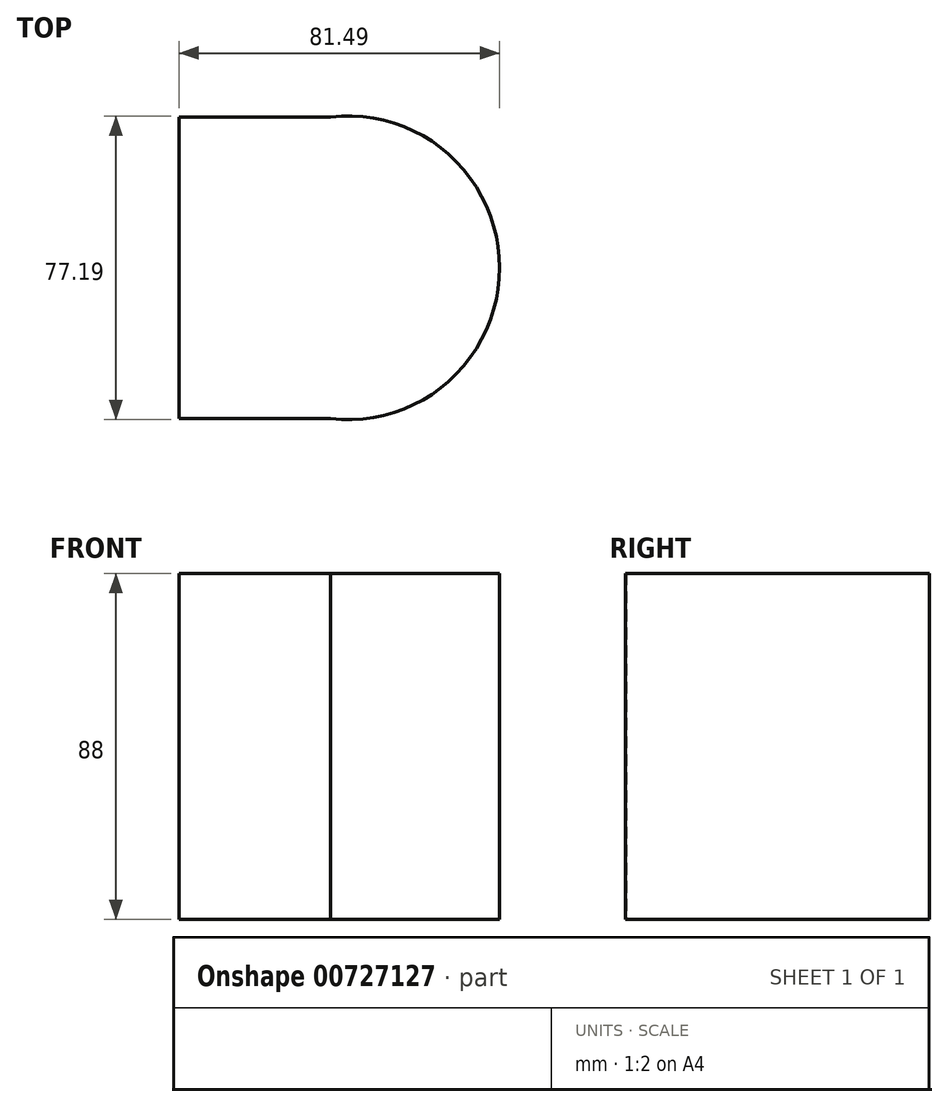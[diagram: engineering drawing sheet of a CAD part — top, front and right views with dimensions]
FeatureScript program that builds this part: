
annotation { "Feature Type Name" : "Feature", "Feature Type Description" : "" }
export const myFeature = defineFeature(function(context is Context, id is Id, definition is map)
    precondition{}
    {
        {
            var Q0;
            Q0=qCreatedBy(makeId("Top.planeOp"),FACE);
            var sketch = newSketch(context, id + "F0", { "sketchPlane" : qUnion([Q0])});
            skLineSegment(sketch, "E0.bottom", {"start": v(0, 0) * mm, "end": v(42.9, 0) * mm});
            skLineSegment(sketch, "E0.top", {"start": v(0, 76.7) * mm, "end": v(42.9, 76.7) * mm});
            skLineSegment(sketch, "E0.left", {"start": v(0, 0) * mm, "end": v(0, 76.7) * mm});
            skCircle(sketch, "E1", {"center": v(42.9, 38.35) * mm, "radius": 28.43 * mm});
            skArc(sketch, "E2", {"start": v(38.54, 0) * mm, "mid": v(81.49, 38.35) * mm, "end": v(38.54, 76.7) * mm});
            skSolve(sketch);
        }
        {
            var Q0;
            Q0=makeQuery(id+"F0.imprint","IMPRINT",FACE,{"disambiguationData":[TD([[makeQuery(id+"F0.imprint","IMPRINT",EDGE,{"derivedFrom":sQuery(id+"F0.wireOp",EDGE,"E1")}),1.0]])]});
            var Q1;
            {var subQ0=sQuery(id+"F0.wireOp",EDGE,"E0.left");Q1=makeQuery(id+"F0.imprint","IMPRINT",FACE,{"disambiguationData":[TD([[makeQuery(id+"F0.imprint","IMPRINT",EDGE,{"derivedFrom":subQ0}),-1.0]])]});}
            extrude(context, id + "F1", {"entities" : qUnion([Q0, Q1]), "depth" : 88 * mm, "offsetDistance" : 25 * mm});
        }
    });
